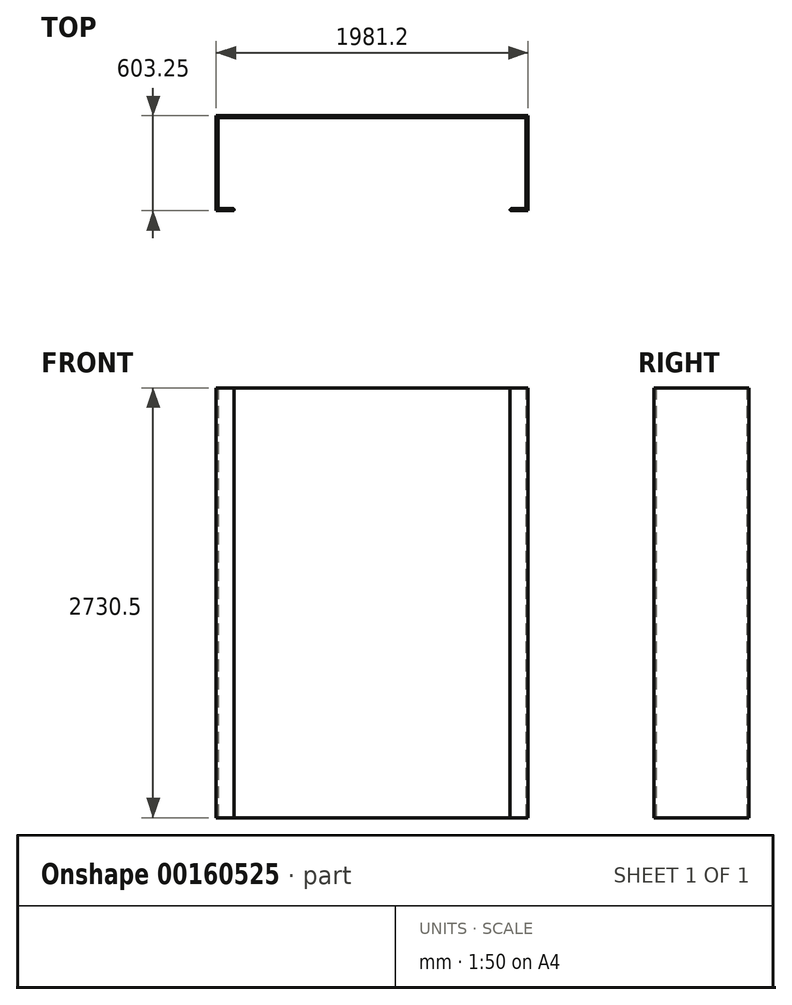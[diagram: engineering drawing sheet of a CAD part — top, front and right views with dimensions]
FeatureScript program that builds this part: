
annotation { "Feature Type Name" : "Feature", "Feature Type Description" : "" }
export const myFeature = defineFeature(function(context is Context, id is Id, definition is map)
    precondition{}
    {
        {
            var Q0;
            Q0=qCreatedBy(makeId("Top.planeOp"),FACE);
            var sketch = newSketch(context, id + "F0", { "sketchPlane" : qUnion([Q0])});
            skLineSegment(sketch, "E0.bottom", {"start": v(-1002.33, 33) * mm, "end": v(953.47, 33) * mm});
            skLineSegment(sketch, "E0.left", {"start": v(-1002.33, 33) * mm, "end": v(-1002.33, -544.85) * mm});
            skLineSegment(sketch, "E0.right", {"start": v(953.47, 33) * mm, "end": v(953.47, -544.85) * mm});
            skLineSegment(sketch, "E1", {"start": v(953.47, -544.85) * mm, "end": v(858.22, -544.85) * mm});
            skLineSegment(sketch, "E2", {"start": v(-1002.33, -544.85) * mm, "end": v(-907.08, -544.85) * mm});
            skLineSegment(sketch, "E3.0", {"start": v(-1002.33, 45.7) * mm, "end": v(953.47, 45.7) * mm});
            skLineSegment(sketch, "E4.0", {"start": v(966.17, 33) * mm, "end": v(966.17, -544.85) * mm});
            skLineSegment(sketch, "E5.0", {"start": v(-1015.03, 33) * mm, "end": v(-1015.03, -544.85) * mm});
            skLineSegment(sketch, "E6.0", {"start": v(953.47, -557.55) * mm, "end": v(858.22, -557.55) * mm});
            skLineSegment(sketch, "E7.0", {"start": v(-1002.33, -557.55) * mm, "end": v(-907.08, -557.55) * mm});
            skLineSegment(sketch, "E8", {"start": v(-900.73, -551.2) * mm, "end": v(-900.73, -551.2) * mm});
            skLineSegment(sketch, "E9", {"start": v(-1002.33, -557.55) * mm, "end": v(-1015.03, -557.55) * mm});
            skLineSegment(sketch, "E10", {"start": v(-1015.03, -544.85) * mm, "end": v(-1015.03, -557.55) * mm});
            skLineSegment(sketch, "E11", {"start": v(-1002.33, 45.7) * mm, "end": v(-1015.03, 45.7) * mm});
            skLineSegment(sketch, "E12", {"start": v(-1015.03, 33) * mm, "end": v(-1015.03, 45.7) * mm});
            skLineSegment(sketch, "E13", {"start": v(966.17, 33) * mm, "end": v(966.17, 45.7) * mm});
            skLineSegment(sketch, "E14", {"start": v(953.47, 45.7) * mm, "end": v(966.17, 45.7) * mm});
            skLineSegment(sketch, "E15", {"start": v(966.17, -544.85) * mm, "end": v(966.17, -557.55) * mm});
            skLineSegment(sketch, "E16", {"start": v(953.47, -557.55) * mm, "end": v(966.17, -557.55) * mm});
            skLineSegment(sketch, "E17", {"start": v(851.87, -551.2) * mm, "end": v(851.87, -551.2) * mm});
            skPoint(sketch, "E18.visualSharp", {"position": v(851.87, -557.55) * mm});
            skArc(sketch, "E18.filletArc", {"start": v(851.87, -551.2) * mm, "mid": v(853.73, -555.69) * mm, "end": v(858.22, -557.55) * mm});
            skPoint(sketch, "E19.visualSharp", {"position": v(851.87, -544.85) * mm});
            skArc(sketch, "E19.filletArc", {"start": v(858.22, -544.85) * mm, "mid": v(853.73, -546.7) * mm, "end": v(851.87, -551.2) * mm});
            skPoint(sketch, "E20.visualSharp", {"position": v(-900.73, -544.85) * mm});
            skArc(sketch, "E20.filletArc", {"start": v(-900.73, -551.2) * mm, "mid": v(-902.6, -546.7) * mm, "end": v(-907.08, -544.85) * mm});
            skPoint(sketch, "E21.visualSharp", {"position": v(-900.73, -557.55) * mm});
            skArc(sketch, "E21.filletArc", {"start": v(-907.08, -557.55) * mm, "mid": v(-902.6, -555.69) * mm, "end": v(-900.73, -551.2) * mm});
            skSolve(sketch);
        }
        {
            var Q0;
            Q0=makeQuery(id+"F0.imprint","IMPRINT",FACE,{"disambiguationData":[TD([[makeQuery(id+"F0.imprint","IMPRINT",EDGE,{"derivedFrom":sQuery(id+"F0.wireOp",EDGE,"E0.bottom")}),-1.0]])]});
            var Q1;
            Q1=makeQuery(id+"F0.imprint","IMPRINT",FACE,{"disambiguationData":[TD([[makeQuery(id+"F0.imprint","IMPRINT",EDGE,{"derivedFrom":sQuery(id+"F0.wireOp",EDGE,"E0.bottom")}),1.0]])]});
            extrude(context, id + "F1", {"entities" : qUnion([Q0, Q1]), "depth" : 2730.5 * mm});
        }
    });
